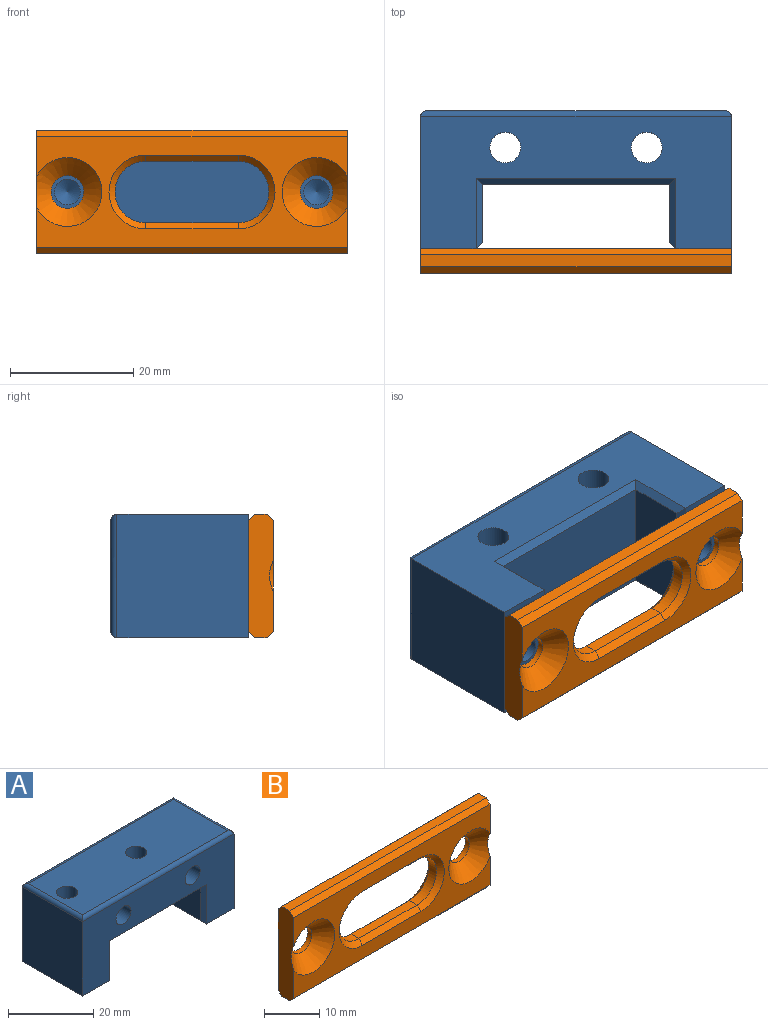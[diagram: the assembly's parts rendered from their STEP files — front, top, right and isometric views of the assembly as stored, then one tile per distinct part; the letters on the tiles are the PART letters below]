
ASSEMBLY  parts=2 mates=1
PART A: 34 faces, bbox 50.5x20x22.4 mm
  f0: plane 21.4x20mm, normal (-1,0,0), area 428mm2, adj f1,f8,f9,f30
  f1: plane 20x9mm, normal (0,0,-1), area 166.1mm2, adj f0,f8,f9,f15,f24
  f2: plane 18x9.4mm, normal (1,0,0), area 169.2mm2, adj f3,f22,f24,f26
  f3: plane 30.5x18mm, normal (0,0,-1), area 549mm2, adj f2,f4,f23,f28
  f4: plane 18x9.4mm, normal (-1,0,0), area 169.2mm2, adj f3,f25,f27,f29
  f5: plane 20x9mm, normal (0,0,-1), area 166.1mm2, adj f6,f8,f9,f13,f27
  f6: plane 21.4x20mm, normal (1,0,0), area 408.4mm2, adj f5,f8,f9,f11,f33
  f7: plane 48.5x18mm, normal (0,0,1), area 833.7mm2, adj f19,f21,f30,f31,f32,f33
  f8: plane 50.5x21.4mm, normal (0,-1,0), area 670.9mm2, adj f0,f1,f5,f6,f16,f17,f22,f23
  f9: plane 50.5x21.4mm, normal (0,1,0), area 670.9mm2, adj f0,f1,f5,f6,f16,f17,f26,f28
  f10: cone r=0mm half-angle=59deg, axis (1,0,0), area 22.9mm2, adj f11
  f11: cylinder r=2.5mm len=8mm, axis (1,0,0), area 125.7mm2, adj f6,f10
  f12: cone r=0mm half-angle=59deg, axis (0,0,-1), area 16.2mm2, adj f13
  f13: cylinder r=2.1mm len=9.2mm, axis (0,0,-1), area 121.4mm2, adj f5,f12
  f14: cone r=0mm half-angle=59deg, axis (0,0,-1), area 16.2mm2, adj f15
  f15: cylinder r=2.1mm len=9.2mm, axis (0,0,-1), area 121.4mm2, adj f1,f14
  f16: cylinder r=2.5mm len=20mm, axis (0,-1,0), area 314.2mm2, adj f8,f9
  f17: cylinder r=2.5mm len=20mm, axis (0,-1,0), area 314.2mm2, adj f8,f9
  f18: cone r=0mm half-angle=59deg, axis (0,0,1), area 22.9mm2, adj f19
  f19: cylinder r=2.5mm len=9mm, axis (0,0,1), area 141.4mm2, adj f7,f18
  f20: cone r=0mm half-angle=59deg, axis (0,0,1), area 22.9mm2, adj f21
  f21: cylinder r=2.5mm len=9mm, axis (0,0,1), area 141.4mm2, adj f7,f20
  f22: plane 11.4x1mm, normal (0.71,-0.71,0), area 14.7mm2, adj f2,f8,f23,f24
  f23: plane 32.5x1mm, normal (0,-0.71,-0.71), area 44.5mm2, adj f3,f8,f22,f25
  f24: plane 20x1mm, normal (0.71,0,-0.71), area 26.9mm2, adj f1,f2,f22,f26
  f25: plane 11.4x1mm, normal (-0.71,-0.71,0), area 14.7mm2, adj f4,f8,f23,f27
  f26: plane 11.4x1mm, normal (0.71,0.71,0), area 14.7mm2, adj f2,f9,f24,f28
  f27: plane 20x1mm, normal (-0.71,0,-0.71), area 26.9mm2, adj f4,f5,f25,f29
  f28: plane 32.5x1mm, normal (0,0.71,-0.71), area 44.5mm2, adj f3,f9,f26,f29
  f29: plane 11.4x1mm, normal (-0.71,0.71,0), area 14.7mm2, adj f4,f9,f27,f28
  f30: cylinder r=1mm len=20mm, axis (0,1,0), area 30.3mm2, adj f0,f7,f31,f32
  f31: cylinder r=1mm len=50.5mm, axis (1,0,0), area 78.2mm2, adj f7,f8,f30,f33
  f32: cylinder r=1mm len=50.5mm, axis (-1,0,0), area 78.2mm2, adj f7,f9,f30,f33
  f33: cylinder r=1mm len=20mm, axis (0,1,0), area 30.3mm2, adj f6,f7,f31,f32
PART B: 26 faces, bbox 51.7x4x20 mm
  f0: plane 50.5x18mm, normal (0,-1,0), area 422.9mm2, adj f2,f3,f7,f8,f18,f19,f20,f21
  f1: plane 50.5x18mm, normal (0,1,0), area 571.8mm2, adj f2,f3,f6,f9,f14,f15,f16,f17
  f2: plane 20x4mm, normal (-1,0,0), area 76mm2, adj f0,f1,f4,f5,f8,f22,f23,f24
  f3: plane 20x4mm, normal (1,0,0), area 76mm2, adj f0,f1,f4,f5,f7,f22,f23,f24
  f4: plane 50.5x2mm, normal (0,0,1), area 101mm2, adj f2,f3,f22,f24
  f5: plane 50.5x2mm, normal (0,0,-1), area 101mm2, adj f2,f3,f23,f25
  f6: cylinder r=2.65mm len=5.3mm, axis (0,-1,0), area 17.5mm2, adj f1,f7
  f7: cone r=2.65mm half-angle=45deg, axis (0,-1,0), area 105.2mm2, adj f0,f3,f6
  f8: cone r=2.65mm half-angle=45deg, axis (0,-1,0), area 105.2mm2, adj f0,f2,f9
  f9: cylinder r=2.65mm len=5.3mm, axis (0,-1,0), area 17.5mm2, adj f1,f8
  f10: plane 15x2mm, normal (0,0,-1), area 30mm2, adj f11,f13,f17,f21
  f11: cylinder r=5mm len=10mm, axis (0,-1,0), area 31.4mm2, adj f10,f12,f15,f19
  f12: plane 15x2mm, normal (0,0,1), area 30mm2, adj f11,f13,f14,f18
  f13: cylinder r=5mm len=10mm, axis (0,-1,0), area 31.4mm2, adj f10,f12,f16,f20
  f14: plane 15x1mm, normal (0,0.71,0.71), area 21.2mm2, adj f1,f12,f15,f16
  f15: cone r=6mm half-angle=45deg, axis (0,1,0), area 24.4mm2, adj f1,f11,f14,f17
  f16: cone r=6mm half-angle=45deg, axis (0,1,0), area 24.4mm2, adj f1,f13,f14,f17
  f17: plane 15x1mm, normal (0,0.71,-0.71), area 21.2mm2, adj f1,f10,f15,f16
  f18: plane 15x1mm, normal (0,-0.71,0.71), area 21.2mm2, adj f0,f12,f19,f20
  f19: cone r=5mm half-angle=45deg, axis (0,-1,0), area 24.4mm2, adj f0,f11,f18,f21
  f20: cone r=5mm half-angle=45deg, axis (0,-1,0), area 24.4mm2, adj f0,f13,f18,f21
  f21: plane 15x1mm, normal (0,-0.71,-0.71), area 21.2mm2, adj f0,f10,f19,f20
  f22: plane 50.5x1mm, normal (0,0.71,0.71), area 71.4mm2, adj f1,f2,f3,f4
  f23: plane 50.5x1mm, normal (0,0.71,-0.71), area 71.4mm2, adj f1,f2,f3,f5
  f24: plane 50.5x1mm, normal (0,-0.71,0.71), area 71.4mm2, adj f0,f2,f3,f4
  f25: plane 50.5x1mm, normal (0,-0.71,-0.71), area 71.4mm2, adj f0,f2,f3,f5
PLACE A rot(axis=(-1,0,0),90deg) t=(5.37,37.17,-15.84)mm
PLACE B t=(5.37,14.77,-5.84)mm
MATE planar A.f5 <-> B.f1  axis (0,-1,0) through (26.16,14.77,-15.84)mm
